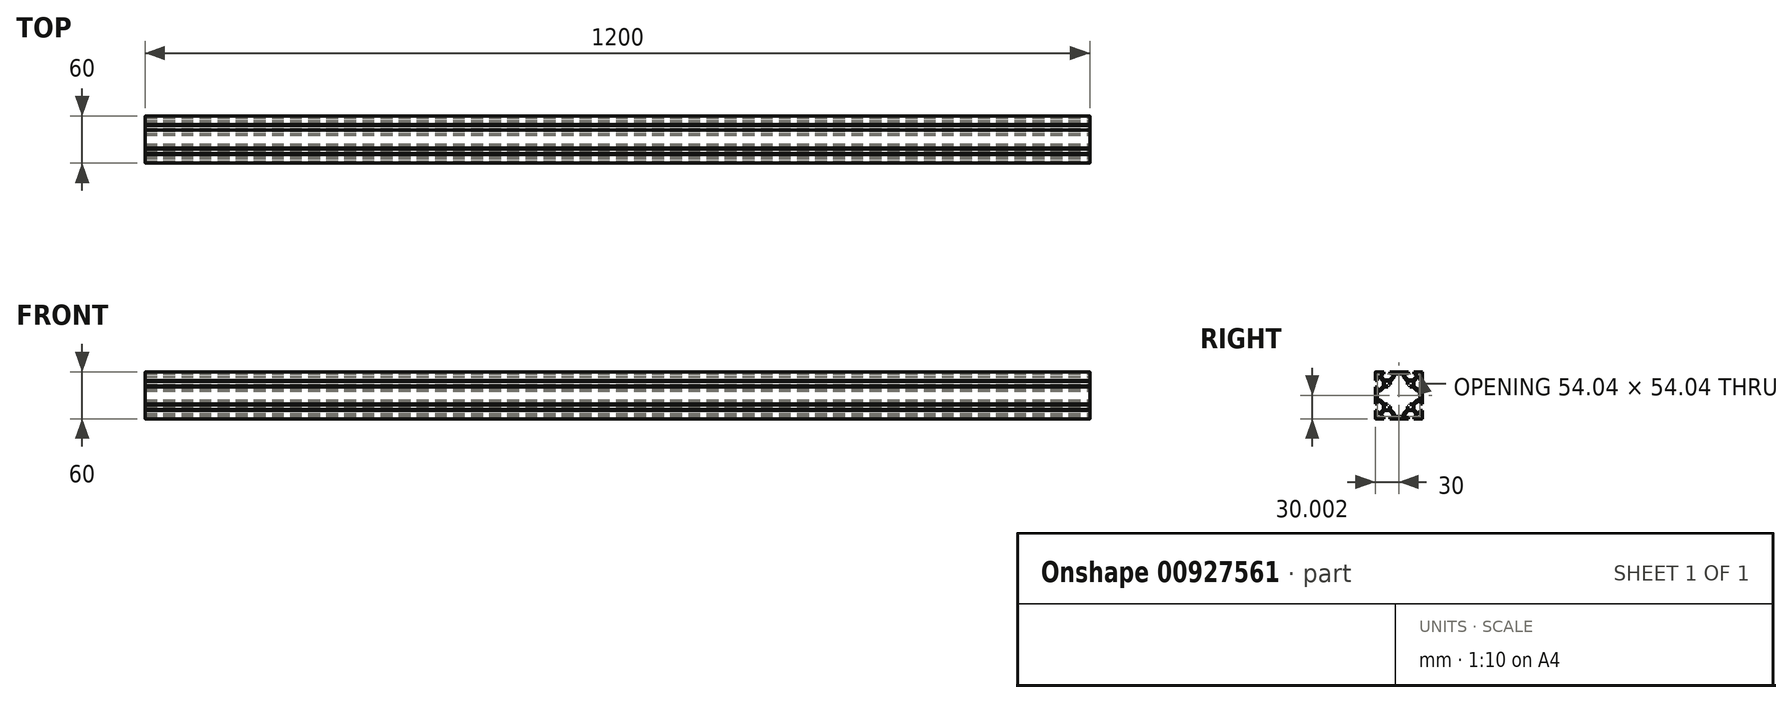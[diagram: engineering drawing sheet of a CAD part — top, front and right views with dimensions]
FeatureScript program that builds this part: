
annotation { "Feature Type Name" : "Feature", "Feature Type Description" : "" }
export const myFeature = defineFeature(function(context is Context, id is Id, definition is map)
    precondition{}
    {
        {
            var Q0;
            Q0=qCreatedBy(makeId("Right.planeOp"),FACE);
            var sketch = newSketch(context, id + "F0", { "sketchPlane" : qUnion([Q0])});
            skLineSegment(sketch, "E0", {"start": v(-22.32, 116.05) * mm, "end": v(-22.32, 37.16) * mm, "construction": true});
            skLineSegment(sketch, "E1.MirrorCS", {"start": v(-52.32, 116.05) * mm, "end": v(-52.32, 37.16) * mm, "construction": true});
            skLineSegment(sketch, "E2.MirrorCS", {"start": v(-78.06, 57.36) * mm, "end": v(13.42, 57.36) * mm, "construction": true});
            skLineSegment(sketch, "E3.0", {"start": v(-7.32, 102.36) * mm, "end": v(-7.32, 91.38) * mm});
            skLineSegment(sketch, "E4.MirrorCS", {"start": v(-67.32, 102.36) * mm, "end": v(-67.32, 91.36) * mm});
            skLineSegment(sketch, "E5.0", {"start": v(-67.32, 42.36) * mm, "end": v(-56.32, 42.36) * mm});
            skLineSegment(sketch, "E6.MirrorCS", {"start": v(-67.32, 102.36) * mm, "end": v(-56.32, 102.36) * mm});
            skPoint(sketch, "E7", {"position": v(-52.32, 87.36) * mm});
            skPoint(sketch, "E8", {"position": v(-22.32, 87.36) * mm});
            skPoint(sketch, "E9", {"position": v(-22.32, 57.36) * mm});
            skPoint(sketch, "E10", {"position": v(-52.32, 57.36) * mm});
            skArc(sketch, "E11", {"start": v(-49.07, 86.36) * mm, "mid": v(-54.72, 89.77) * mm, "end": v(-51.32, 84.11) * mm});
            skArc(sketch, "E12", {"start": v(-23.32, 84.11) * mm, "mid": v(-19.92, 89.77) * mm, "end": v(-25.57, 86.36) * mm});
            skArc(sketch, "E13", {"start": v(-52.03, 60.75) * mm, "mid": v(-54.45, 54.72) * mm, "end": v(-49.07, 58.36) * mm});
            skArc(sketch, "E14", {"start": v(-25.57, 58.36) * mm, "mid": v(-19.92, 54.96) * mm, "end": v(-23.32, 60.61) * mm});
            skLineSegment(sketch, "E15", {"start": v(-56.32, 102.36) * mm, "end": v(-56.32, 99.45) * mm});
            skLineSegment(sketch, "E16", {"start": v(-67.32, 91.36) * mm, "end": v(-64.4, 91.36) * mm});
            skLineSegment(sketch, "E17", {"start": v(-56.32, 99.45) * mm, "end": v(-59.63, 99.45) * mm});
            skLineSegment(sketch, "E18", {"start": v(-64.4, 91.36) * mm, "end": v(-64.4, 95.63) * mm});
            skLineSegment(sketch, "E19", {"start": v(-61.66, 95.63) * mm, "end": v(-56.7, 90.33) * mm});
            skLineSegment(sketch, "E20.MirrorCS", {"start": v(-59.63, 96.4) * mm, "end": v(-55.3, 91.75) * mm});
            skLineSegment(sketch, "E21", {"start": v(-64.4, 95.63) * mm, "end": v(-61.66, 95.63) * mm});
            skLineSegment(sketch, "E22", {"start": v(-59.63, 96.4) * mm, "end": v(-59.63, 99.45) * mm});
            skLineSegment(sketch, "E23", {"start": v(-48.32, 102.36) * mm, "end": v(-48.32, 100.36) * mm});
            skLineSegment(sketch, "E24", {"start": v(-25.38, 102.36) * mm, "end": v(-25.38, 100.32) * mm});
            skLineSegment(sketch, "E25", {"start": v(-25.38, 100.32) * mm, "end": v(-29.63, 100.32) * mm});
            skLineSegment(sketch, "E26", {"start": v(-48.32, 100.36) * mm, "end": v(-45, 100.36) * mm});
            skLineSegment(sketch, "E27.trimOffspring", {"start": v(-48.32, 102.36) * mm, "end": v(-25.38, 102.36) * mm});
            skLineSegment(sketch, "E28.MirrorCS", {"start": v(-15, 96.4) * mm, "end": v(-19.35, 91.75) * mm});
            skLineSegment(sketch, "E29.MirrorCS", {"start": v(-12.98, 95.63) * mm, "end": v(-17.93, 90.33) * mm});
            skLineSegment(sketch, "E30", {"start": v(-18.32, 102.36) * mm, "end": v(-18.32, 99.45) * mm});
            skLineSegment(sketch, "E31", {"start": v(-7.32, 91.38) * mm, "end": v(-10.23, 91.38) * mm});
            skLineSegment(sketch, "E32", {"start": v(-10.23, 91.38) * mm, "end": v(-10.23, 95.63) * mm});
            skLineSegment(sketch, "E33", {"start": v(-12.98, 95.63) * mm, "end": v(-10.23, 95.63) * mm});
            skLineSegment(sketch, "E34", {"start": v(-19.35, 91.75) * mm, "end": v(-23.12, 91.75) * mm});
            skLineSegment(sketch, "E35", {"start": v(-17.93, 90.33) * mm, "end": v(-17.93, 84.24) * mm});
            skLineSegment(sketch, "E36", {"start": v(-42.98, 99.38) * mm, "end": v(-42.98, 95.63) * mm});
            skLineSegment(sketch, "E37.MirrorCS", {"start": v(-45, 96.4) * mm, "end": v(-49.35, 91.75) * mm});
            skLineSegment(sketch, "E38.MirrorCS", {"start": v(-42.98, 95.63) * mm, "end": v(-47.93, 90.33) * mm});
            skLineSegment(sketch, "E39", {"start": v(-47.93, 90.33) * mm, "end": v(-47.93, 86.36) * mm});
            skLineSegment(sketch, "E40.MirrorCS", {"start": v(-26.7, 90.33) * mm, "end": v(-26.7, 86.36) * mm});
            skLineSegment(sketch, "E41.MirrorCS", {"start": v(-31.66, 95.63) * mm, "end": v(-26.7, 90.33) * mm});
            skLineSegment(sketch, "E42.MirrorCS", {"start": v(-29.63, 96.4) * mm, "end": v(-25.3, 91.75) * mm});
            skLineSegment(sketch, "E43.MirrorCS", {"start": v(-31.66, 99.38) * mm, "end": v(-31.66, 95.63) * mm});
            skLineSegment(sketch, "E44", {"start": v(-29.63, 96.4) * mm, "end": v(-29.63, 99.32) * mm});
            skLineSegment(sketch, "E45", {"start": v(-42.98, 99.38) * mm, "end": v(-31.66, 99.38) * mm});
            skLineSegment(sketch, "E46.trimOffspring", {"start": v(-18.32, 102.36) * mm, "end": v(-7.32, 102.36) * mm});
            skLineSegment(sketch, "E47", {"start": v(-45, 100.36) * mm, "end": v(-45, 96.4) * mm});
            skLineSegment(sketch, "E48", {"start": v(-25.3, 91.75) * mm, "end": v(-23.12, 91.75) * mm});
            skLineSegment(sketch, "E49", {"start": v(-15, 99.45) * mm, "end": v(-15, 96.4) * mm});
            skLineSegment(sketch, "E50", {"start": v(-18.32, 99.45) * mm, "end": v(-15, 99.45) * mm});
            skLineSegment(sketch, "E51", {"start": v(-29.63, 99.32) * mm, "end": v(-29.63, 100.32) * mm});
            skLineSegment(sketch, "E52.MirrorCS", {"start": v(-64.4, 53.36) * mm, "end": v(-64.4, 49.09) * mm});
            skLineSegment(sketch, "E53.MirrorCS", {"start": v(-64.4, 49.09) * mm, "end": v(-61.66, 49.09) * mm});
            skLineSegment(sketch, "E54.MirrorCS", {"start": v(-61.66, 49.09) * mm, "end": v(-56.7, 54.39) * mm});
            skLineSegment(sketch, "E55.MirrorCS", {"start": v(-56.32, 42.36) * mm, "end": v(-56.32, 45.27) * mm});
            skLineSegment(sketch, "E56.MirrorCS", {"start": v(-56.32, 45.27) * mm, "end": v(-59.63, 45.27) * mm});
            skLineSegment(sketch, "E57.MirrorCS", {"start": v(-59.63, 48.33) * mm, "end": v(-59.63, 45.27) * mm});
            skLineSegment(sketch, "E58.MirrorCS", {"start": v(-59.63, 48.33) * mm, "end": v(-55.3, 52.97) * mm});
            skLineSegment(sketch, "E59.MirrorCS", {"start": v(-55.3, 52.97) * mm, "end": v(-45.12, 52.97) * mm});
            skLineSegment(sketch, "E60.MirrorCS", {"start": v(-55.3, 52.97) * mm, "end": v(-49.35, 52.97) * mm});
            skLineSegment(sketch, "E61.MirrorCS", {"start": v(-45, 48.33) * mm, "end": v(-49.35, 52.97) * mm});
            skLineSegment(sketch, "E62.MirrorCS", {"start": v(-45, 44.36) * mm, "end": v(-45, 48.33) * mm});
            skLineSegment(sketch, "E63.MirrorCS", {"start": v(-48.32, 44.36) * mm, "end": v(-45, 44.36) * mm});
            skLineSegment(sketch, "E64.MirrorCS", {"start": v(-48.32, 42.36) * mm, "end": v(-48.32, 44.36) * mm});
            skLineSegment(sketch, "E65.MirrorCS", {"start": v(-48.32, 42.36) * mm, "end": v(-25.38, 42.36) * mm});
            skLineSegment(sketch, "E66.MirrorCS", {"start": v(-25.38, 42.36) * mm, "end": v(-25.38, 44.4) * mm});
            skLineSegment(sketch, "E67.MirrorCS", {"start": v(-25.38, 44.4) * mm, "end": v(-29.63, 44.4) * mm});
            skLineSegment(sketch, "E68.MirrorCS", {"start": v(-31.66, 45.34) * mm, "end": v(-31.66, 49.09) * mm});
            skLineSegment(sketch, "E69.MirrorCS", {"start": v(-31.66, 49.09) * mm, "end": v(-26.7, 54.39) * mm});
            skLineSegment(sketch, "E70.MirrorCS", {"start": v(-26.7, 54.39) * mm, "end": v(-26.7, 58.36) * mm});
            skLineSegment(sketch, "E71.MirrorCS", {"start": v(-29.63, 45.4) * mm, "end": v(-29.63, 44.4) * mm});
            skLineSegment(sketch, "E72.MirrorCS", {"start": v(-29.63, 48.33) * mm, "end": v(-29.63, 45.4) * mm});
            skLineSegment(sketch, "E73.MirrorCS", {"start": v(-29.63, 48.33) * mm, "end": v(-25.3, 52.97) * mm});
            skLineSegment(sketch, "E74.MirrorCS", {"start": v(-25.3, 52.97) * mm, "end": v(-23.12, 52.97) * mm});
            skLineSegment(sketch, "E75.MirrorCS", {"start": v(-42.98, 45.34) * mm, "end": v(-31.66, 45.34) * mm});
            skLineSegment(sketch, "E76.MirrorCS", {"start": v(-42.98, 45.34) * mm, "end": v(-42.98, 49.09) * mm});
            skLineSegment(sketch, "E77.MirrorCS", {"start": v(-42.98, 49.09) * mm, "end": v(-47.93, 54.39) * mm});
            skLineSegment(sketch, "E78.MirrorCS", {"start": v(-47.93, 54.39) * mm, "end": v(-47.93, 58.36) * mm});
            skLineSegment(sketch, "E79.MirrorCS", {"start": v(-19.35, 52.97) * mm, "end": v(-23.12, 52.97) * mm});
            skLineSegment(sketch, "E80.MirrorCS", {"start": v(-15, 48.33) * mm, "end": v(-19.35, 52.97) * mm});
            skLineSegment(sketch, "E81.MirrorCS", {"start": v(-15, 45.27) * mm, "end": v(-15, 48.33) * mm});
            skLineSegment(sketch, "E82.MirrorCS", {"start": v(-18.32, 45.27) * mm, "end": v(-15, 45.27) * mm});
            skLineSegment(sketch, "E83.MirrorCS", {"start": v(-18.32, 42.36) * mm, "end": v(-18.32, 45.27) * mm});
            skLineSegment(sketch, "E84.MirrorCS", {"start": v(-18.32, 42.36) * mm, "end": v(-7.32, 42.36) * mm});
            skLineSegment(sketch, "E85.MirrorCS", {"start": v(-7.32, 53.34) * mm, "end": v(-10.23, 53.34) * mm});
            skLineSegment(sketch, "E86.MirrorCS", {"start": v(-10.23, 53.34) * mm, "end": v(-10.23, 49.09) * mm});
            skLineSegment(sketch, "E87.MirrorCS", {"start": v(-12.98, 49.09) * mm, "end": v(-10.23, 49.09) * mm});
            skLineSegment(sketch, "E88.MirrorCS", {"start": v(-12.98, 49.09) * mm, "end": v(-17.93, 54.39) * mm});
            skLineSegment(sketch, "E89.MirrorCS", {"start": v(-17.93, 54.39) * mm, "end": v(-17.93, 60.48) * mm});
            skLineSegment(sketch, "E90", {"start": v(-67.32, 102.36) * mm, "end": v(-7.32, 42.36) * mm, "construction": true});
            skLineSegment(sketch, "E91.MirrorCS", {"start": v(-67.32, 83.36) * mm, "end": v(-65.32, 83.36) * mm});
            skLineSegment(sketch, "E92.MirrorCS", {"start": v(-65.32, 83.36) * mm, "end": v(-65.32, 80.05) * mm});
            skLineSegment(sketch, "E93.MirrorCS", {"start": v(-65.32, 80.05) * mm, "end": v(-61.35, 80.05) * mm});
            skLineSegment(sketch, "E94", {"start": v(-7.32, 102.36) * mm, "end": v(-67.32, 42.36) * mm, "construction": true});
            skLineSegment(sketch, "E95.MirrorCS", {"start": v(-67.32, 53.36) * mm, "end": v(-64.4, 53.36) * mm});
            skLineSegment(sketch, "E96.MirrorCS", {"start": v(-67.32, 61.36) * mm, "end": v(-65.32, 61.36) * mm});
            skLineSegment(sketch, "E97.MirrorCS", {"start": v(-65.32, 61.36) * mm, "end": v(-65.32, 64.67) * mm});
            skLineSegment(sketch, "E98.MirrorCS", {"start": v(-65.32, 64.67) * mm, "end": v(-61.35, 64.67) * mm});
            skLineSegment(sketch, "E99.MirrorCS", {"start": v(-61.35, 64.67) * mm, "end": v(-56.7, 60.33) * mm});
            skLineSegment(sketch, "E100.MirrorCS", {"start": v(-56.7, 54.39) * mm, "end": v(-56.7, 60.33) * mm});
            skLineSegment(sketch, "E101.MirrorCS", {"start": v(-64.34, 66.7) * mm, "end": v(-64.34, 78.02) * mm});
            skLineSegment(sketch, "E102.MirrorCS", {"start": v(-64.34, 66.7) * mm, "end": v(-60.6, 66.7) * mm});
            skLineSegment(sketch, "E103.MirrorCS", {"start": v(-60.6, 66.7) * mm, "end": v(-55.3, 61.75) * mm});
            skLineSegment(sketch, "E104.MirrorCS", {"start": v(-55.3, 61.75) * mm, "end": v(-52.03, 61.75) * mm});
            skLineSegment(sketch, "E105.MirrorCS", {"start": v(-60.6, 78.02) * mm, "end": v(-55.3, 82.97) * mm});
            skLineSegment(sketch, "E106", {"start": v(-55.3, 91.75) * mm, "end": v(-49.35, 91.75) * mm});
            skLineSegment(sketch, "E107.MirrorCS", {"start": v(-61.35, 80.05) * mm, "end": v(-56.7, 84.39) * mm});
            skLineSegment(sketch, "E108.MirrorCS", {"start": v(-55.3, 82.97) * mm, "end": v(-51.32, 82.97) * mm});
            skLineSegment(sketch, "E109", {"start": v(-56.7, 90.33) * mm, "end": v(-56.7, 84.39) * mm});
            skLineSegment(sketch, "E110", {"start": v(-64.34, 78.02) * mm, "end": v(-60.6, 78.02) * mm});
            skLineSegment(sketch, "E111.MirrorCS", {"start": v(-10.3, 66.7) * mm, "end": v(-10.3, 78.02) * mm});
            skLineSegment(sketch, "E112.MirrorCS", {"start": v(-7.32, 83.36) * mm, "end": v(-9.32, 83.36) * mm});
            skLineSegment(sketch, "E113.MirrorCS", {"start": v(-9.32, 83.36) * mm, "end": v(-9.32, 80.05) * mm});
            skLineSegment(sketch, "E114.MirrorCS", {"start": v(-9.32, 80.05) * mm, "end": v(-13.29, 80.05) * mm});
            skLineSegment(sketch, "E115.MirrorCS", {"start": v(-14.05, 78.02) * mm, "end": v(-19.35, 82.97) * mm});
            skLineSegment(sketch, "E116.MirrorCS", {"start": v(-19.35, 82.97) * mm, "end": v(-23.32, 82.97) * mm});
            skLineSegment(sketch, "E117.MirrorCS", {"start": v(-10.3, 78.02) * mm, "end": v(-14.05, 78.02) * mm});
            skLineSegment(sketch, "E118.MirrorCS", {"start": v(-10.3, 66.7) * mm, "end": v(-14.05, 66.7) * mm});
            skLineSegment(sketch, "E119.MirrorCS", {"start": v(-14.05, 66.7) * mm, "end": v(-19.35, 61.75) * mm});
            skLineSegment(sketch, "E120.MirrorCS", {"start": v(-19.35, 61.75) * mm, "end": v(-23.32, 61.75) * mm});
            skLineSegment(sketch, "E121.MirrorCS", {"start": v(-7.32, 61.36) * mm, "end": v(-9.32, 61.36) * mm});
            skLineSegment(sketch, "E122.MirrorCS", {"start": v(-9.32, 61.36) * mm, "end": v(-9.32, 64.67) * mm});
            skLineSegment(sketch, "E123.MirrorCS", {"start": v(-9.32, 64.67) * mm, "end": v(-13.29, 64.67) * mm});
            skLineSegment(sketch, "E124.MirrorCS", {"start": v(-13.29, 64.67) * mm, "end": v(-17.93, 60.33) * mm});
            skLineSegment(sketch, "E125.MirrorCS", {"start": v(-13.29, 80.05) * mm, "end": v(-17.93, 84.39) * mm});
            skLineSegment(sketch, "E126.trimOffspring", {"start": v(-67.32, 53.36) * mm, "end": v(-67.32, 42.36) * mm});
            skLineSegment(sketch, "E127.trimOffspring", {"start": v(-7.32, 53.34) * mm, "end": v(-7.32, 42.36) * mm});
            skLineSegment(sketch, "E128.trimOffspring", {"start": v(-7.32, 83.36) * mm, "end": v(-7.32, 61.36) * mm});
            skLineSegment(sketch, "E129.trimOffspring", {"start": v(-67.32, 83.36) * mm, "end": v(-67.32, 61.36) * mm});
            skLineSegment(sketch, "E130", {"start": v(-49.07, 58.36) * mm, "end": v(-47.93, 58.36) * mm});
            skLineSegment(sketch, "E131", {"start": v(-52.03, 61.75) * mm, "end": v(-52.03, 60.75) * mm});
            skLineSegment(sketch, "E132", {"start": v(-51.32, 82.97) * mm, "end": v(-51.32, 84.11) * mm});
            skLineSegment(sketch, "E133", {"start": v(-81.22, 87.36) * mm, "end": v(9.97, 87.36) * mm, "construction": true});
            skLineSegment(sketch, "E134", {"start": v(-49.07, 86.36) * mm, "end": v(-47.93, 86.36) * mm});
            skLineSegment(sketch, "E135", {"start": v(-26.7, 86.36) * mm, "end": v(-25.57, 86.36) * mm});
            skLineSegment(sketch, "E136", {"start": v(-23.32, 84.11) * mm, "end": v(-23.32, 82.97) * mm});
            skLineSegment(sketch, "E137", {"start": v(-26.7, 58.36) * mm, "end": v(-25.57, 58.36) * mm});
            skLineSegment(sketch, "E138", {"start": v(-23.32, 61.75) * mm, "end": v(-23.32, 60.61) * mm});
            skLineSegment(sketch, "E139", {"start": v(-17.93, 60.48) * mm, "end": v(-17.93, 60.33) * mm});
            skLineSegment(sketch, "E140", {"start": v(-17.93, 84.39) * mm, "end": v(-17.93, 84.24) * mm});
            skPoint(sketch, "E141", {"position": v(-37.32, 72.36) * mm});
            skSolve(sketch);
        }
        {
            var Q0;
            Q0 = qSketchRegion(id + "F0", true);
            extrude(context, id + "F1", {"entities" : qUnion([Q0]), "oppositeDirection" : true, "depth" : 1200 * mm, "offsetDistance" : 25 * mm});
        }
        {
            var Q0;
            Q0=makeQuery(id+"F1.opExtrude","SWEPT_EDGE",EDGE,{"disambiguationData":[OSD([sQuery(id+"F0.wireOp",EDGE,"E3.0"),sQuery(id+"F0.wireOp",EDGE,"E46.trimOffspring")])]});
            var Q1;
            Q1=makeQuery(id+"F1.opExtrude","SWEPT_EDGE",EDGE,{"disambiguationData":[OSD([sQuery(id+"F0.wireOp",EDGE,"E4.MirrorCS"),sQuery(id+"F0.wireOp",EDGE,"E6.MirrorCS")])]});
            var Q2;
            Q2=makeQuery(id+"F1.opExtrude","SWEPT_EDGE",EDGE,{"disambiguationData":[OSD([sQuery(id+"F0.wireOp",EDGE,"E84.MirrorCS"),sQuery(id+"F0.wireOp",EDGE,"E127.trimOffspring")])]});
            var Q3;
            Q3=makeQuery(id+"F1.opExtrude","SWEPT_EDGE",EDGE,{"disambiguationData":[OSD([sQuery(id+"F0.wireOp",EDGE,"E5.0"),sQuery(id+"F0.wireOp",EDGE,"E126.trimOffspring")])]});
            fillet(context, id + "F2", {"entities" : qUnion([Q0, Q1, Q2, Q3]), "radius" : 0.5 * mm, "tangentPropagation" : true, "allowEdgeOverflow" : false});
        }
    });
